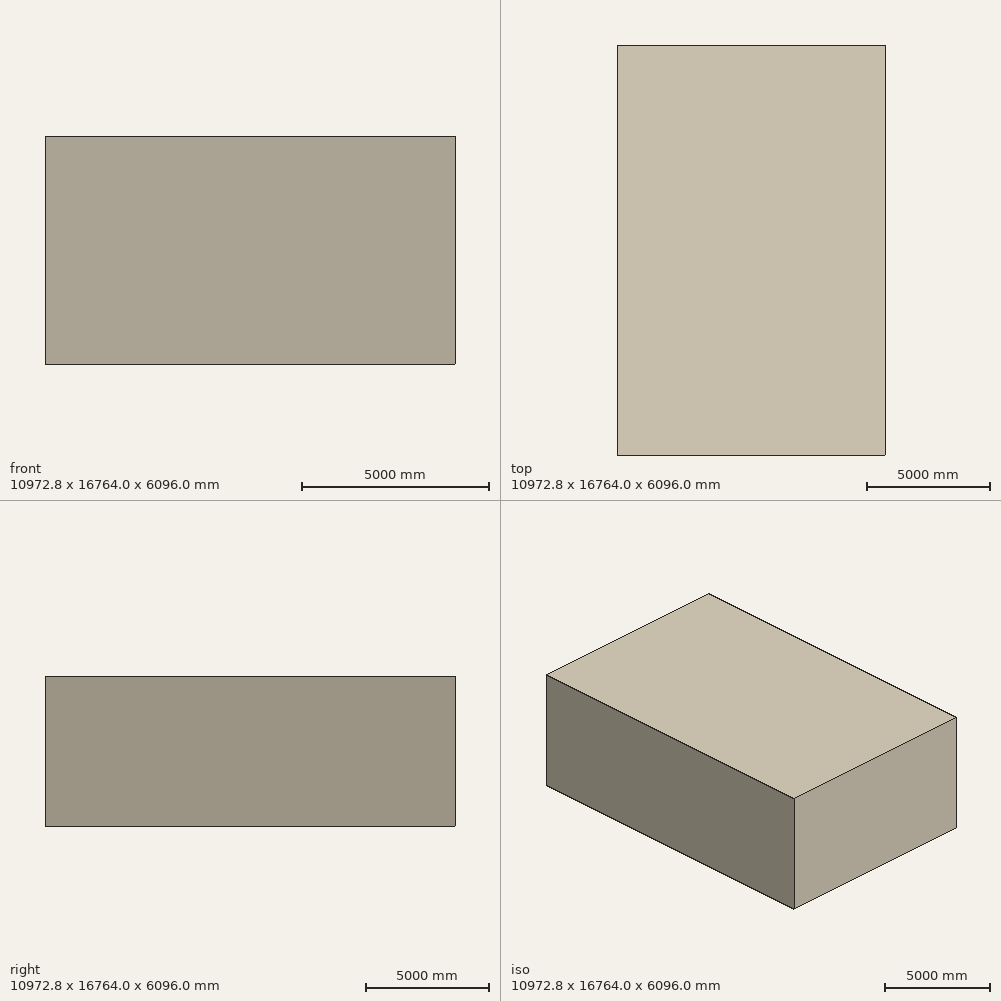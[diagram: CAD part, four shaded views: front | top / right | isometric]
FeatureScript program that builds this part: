
annotation { "Feature Type Name" : "Feature", "Feature Type Description" : "" }
export const myFeature = defineFeature(function(context is Context, id is Id, definition is map)
    precondition{}
    {
        {
            var Q0;
            Q0=qCreatedBy(makeId("Top.planeOp"),FACE);
            var sketch = newSketch(context, id + "F0", { "sketchPlane" : qUnion([Q0])});
            skLineSegment(sketch, "E0.bottom", {"start": v(-5486.4, 8382) * mm, "end": v(5486.4, 8382) * mm});
            skLineSegment(sketch, "E0.top", {"start": v(-5486.4, -8382) * mm, "end": v(5486.4, -8382) * mm});
            skLineSegment(sketch, "E0.left", {"start": v(-5486.4, 8382) * mm, "end": v(-5486.4, -8382) * mm});
            skLineSegment(sketch, "E0.right", {"start": v(5486.4, 8382) * mm, "end": v(5486.4, -8382) * mm});
            skPoint(sketch, "E0.middle", {"position": v(0, 0) * mm});
            skSolve(sketch);
        }
        {
            var Q0;
            Q0 = qSketchRegion(id + "F0", true);
            var Q1;
            Q1 = qBodyType(qCreatedBy(id + "F0" ,EDGE), BodyType.WIRE);
            extrude(context, id + "F1", {"entities" : qUnion([Q0]), "surfaceEntities" : qUnion([Q1]), "oppositeDirection" : true, "depth" : 6096 * mm, "offsetDistance" : 30.48 * mm});
        }
    });
